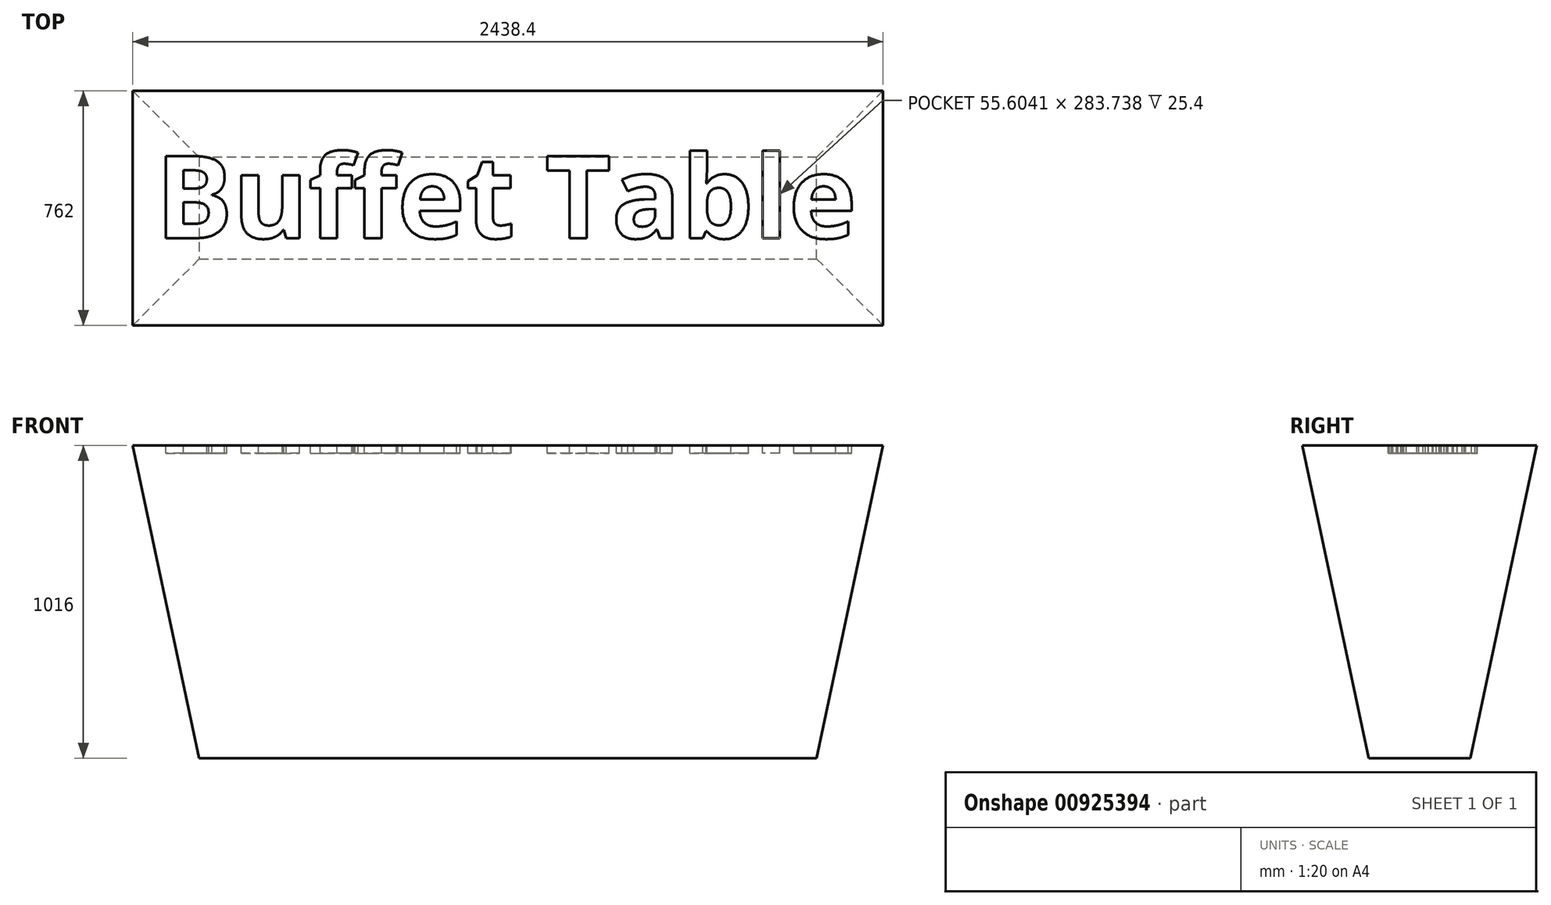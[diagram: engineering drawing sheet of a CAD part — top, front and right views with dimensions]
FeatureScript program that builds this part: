
annotation { "Feature Type Name" : "Feature", "Feature Type Description" : "" }
export const myFeature = defineFeature(function(context is Context, id is Id, definition is map)
    precondition{}
    {
        {
            var Q0;
            Q0=qCreatedBy(makeId("Top.planeOp"),FACE);
            var sketch = newSketch(context, id + "F0", { "sketchPlane" : qUnion([Q0])});
            skLineSegment(sketch, "E0.bottom", {"start": v(1219.2, -381) * mm, "end": v(-1219.2, -381) * mm});
            skLineSegment(sketch, "E0.top", {"start": v(1219.2, 381) * mm, "end": v(-1219.2, 381) * mm});
            skLineSegment(sketch, "E0.left", {"start": v(1219.2, -381) * mm, "end": v(1219.2, 381) * mm});
            skLineSegment(sketch, "E0.right", {"start": v(-1219.2, -381) * mm, "end": v(-1219.2, 381) * mm});
            skPoint(sketch, "E0.middle", {"position": v(0, 0) * mm});
            skSolve(sketch);
        }
        {
            var Q0;
            Q0 = qSketchRegion(id + "F0", true);
            extrude(context, id + "F1", {"entities" : qUnion([Q0]), "oppositeDirection" : true, "depth" : 1016 * mm, "offsetDistance" : 25.4 * mm, "hasDraft" : true, "draftAngle" : 12 * degree, "draftPullDirection" : true});
        }
        {
            var Q0;
            Q0=makeQuery(id+"F1.opExtrude","CAP_FACE",FACE,{"disambiguationData":[OSD([sQuery(id+"F0.wireOp",EDGE,"E0.bottom"),sQuery(id+"F0.wireOp",EDGE,"E0.top"),sQuery(id+"F0.wireOp",EDGE,"E0.left"),sQuery(id+"F0.wireOp",EDGE,"E0.right")])],"isStart":true});
            var sketch = newSketch(context, id + "F2", { "sketchPlane" : qUnion([Q0])});
            skText(sketch, "E1", { "text": "Buffet Table", "fontName": "OpenSans-Bold.ttf"});
            const initialGuessF2  = {"E1": [-1.14495, -0.09735, 1, 0, 0.26886]};
            skSetInitialGuess(sketch, initialGuessF2);
            skSolve(sketch);
        }
        {
            var Q0;
            Q0 = qSketchRegion(id + "F2", true);
            extrude(context, id + "F3", {"entities" : qUnion([Q0]), "operationType" : NewBodyOperationType.REMOVE, "oppositeDirection" : true, "depth" : 25.4 * mm, "offsetDistance" : 25.4 * mm});
        }
    });
